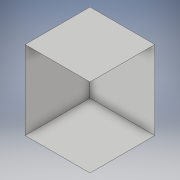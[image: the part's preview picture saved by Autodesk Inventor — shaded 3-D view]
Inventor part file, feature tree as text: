
AUTODESK INVENTOR PART (.ipt)
format: ipt  version: 2017 (Build 210142000, 142)  size: 93,696 bytes
history: native  units: in
note: dims shown in document units (in); Inventor stores cm internally (conversion verified against a paired STEP export)
features: extrude x1, delete_face x1, sketch x1
ambient origin geometry x8: Origin, YZ Plane, XZ Plane, XY Plane, X Axis, Y Axis, Z Axis, Center Point
bodies: Solid1 (feature_tree)
feature tree (3):
  extrude  "Extrusion1"  Depth=8.5in
  delete_face  "Delete Face1"
  sketch  "Sketch1"  dims[d0=8.5in d1=7.0in d2=7.0in d3=0.0in]
